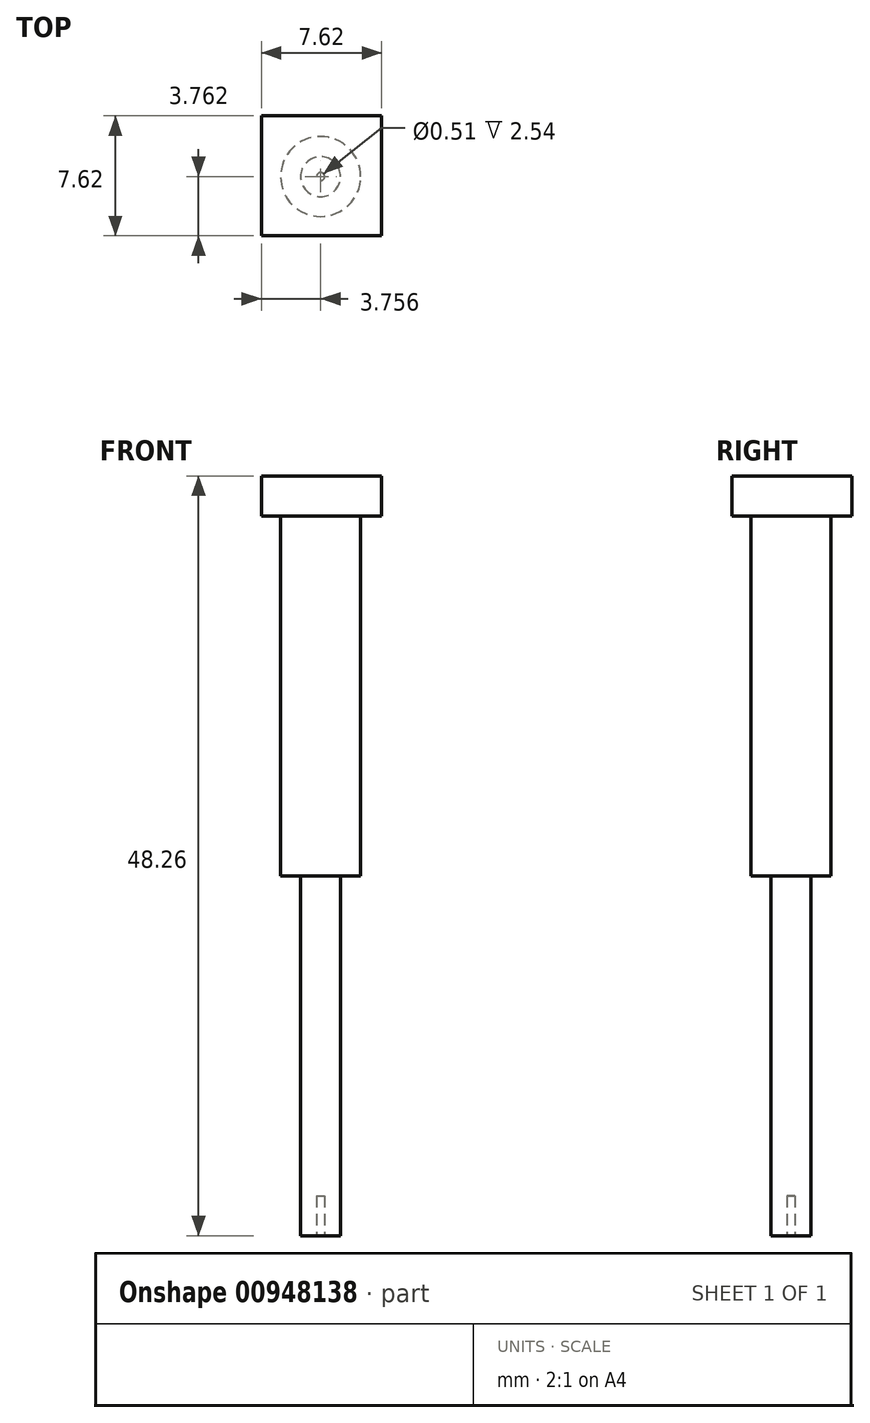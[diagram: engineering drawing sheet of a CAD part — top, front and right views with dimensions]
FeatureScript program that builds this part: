
annotation { "Feature Type Name" : "Feature", "Feature Type Description" : "" }
export const myFeature = defineFeature(function(context is Context, id is Id, definition is map)
    precondition{}
    {
        {
            var Q0;
            Q0=qCreatedBy(makeId("Top.planeOp"),FACE);
            var sketch = newSketch(context, id + "F0", { "sketchPlane" : qUnion([Q0])});
            skLineSegment(sketch, "E0.bottom", {"start": v(-42.6, -18.03) * mm, "end": v(-34.99, -18.03) * mm});
            skLineSegment(sketch, "E0.top", {"start": v(-42.6, -25.65) * mm, "end": v(-34.99, -25.65) * mm});
            skLineSegment(sketch, "E0.left", {"start": v(-42.6, -18.03) * mm, "end": v(-42.6, -25.65) * mm});
            skLineSegment(sketch, "E0.right", {"start": v(-34.99, -18.03) * mm, "end": v(-34.99, -25.65) * mm});
            skSolve(sketch);
        }
        {
            var Q0;
            Q0=qSketchRegion(id+"F0",true);
            var Q1;
            Q1 = qSketchRegion(id + "F2", true);
            extrude(context, id + "F1", {"entities" : qUnion([Q0, Q1]), "depth" : 2.54 * mm, "offsetDistance" : 25.4 * mm});
        }
        {
            var Q0;
            Q0=makeQuery(id+"F1.opExtrude","CAP_FACE",FACE,{"disambiguationData":[OSD([sQuery(id+"F0.wireOp",EDGE,"E0.bottom"),sQuery(id+"F0.wireOp",EDGE,"E0.top"),sQuery(id+"F0.wireOp",EDGE,"E0.left"),sQuery(id+"F0.wireOp",EDGE,"E0.right")])],"isStart":true});
            var sketch = newSketch(context, id + "F2", { "sketchPlane" : qUnion([Q0])});
            skCircle(sketch, "E1", {"center": v(-38.85, 21.89) * mm, "radius": 2.54 * mm});
            skCircle(sketch, "E2", {"center": v(-38.85, 21.89) * mm, "radius": 1.27 * mm});
            skSolve(sketch);
        }
        {
            var Q0;
            Q0=qSketchRegion(id+"F2",true);
            extrude(context, id + "F3", {"entities" : qUnion([Q0]), "operationType" : NewBodyOperationType.ADD, "depth" : 22.86 * mm, "offsetDistance" : 25.4 * mm});
        }
        {
            var Q0;
            Q0=makeQuery(id+"F3.boolean.opBoolean","SPLIT",FACE,{"disambiguationData":[TD([makeQuery(id+"F3.opExtrude","SWEPT_FACE",FACE,{"disambiguationData":[OSD([sQuery(id+"F2.wireOp",EDGE,"E2")])]})])],"derivedFrom":makeQuery(id+"F1.opExtrude","CAP_FACE",FACE,{"disambiguationData":[OSD([sQuery(id+"F0.wireOp",EDGE,"E0.bottom"),sQuery(id+"F0.wireOp",EDGE,"E0.top"),sQuery(id+"F0.wireOp",EDGE,"E0.left"),sQuery(id+"F0.wireOp",EDGE,"E0.right")])],"isStart":true})});
            extrude(context, id + "F4", {"entities" : qUnion([Q0]), "operationType" : NewBodyOperationType.ADD, "depth" : 22.86 * mm, "offsetDistance" : 25.4 * mm});
        }
        {
            var Q0;
            Q0=makeQuery(id+"F2.imprint","IMPRINT",FACE,{"disambiguationData":[TD([[makeQuery(id+"F2.imprint","IMPRINT",EDGE,{"derivedFrom":sQuery(id+"F2.wireOp",EDGE,"E2")}),1.0]])]});
            extrude(context, id + "F5", {"entities" : qUnion([Q0]), "operationType" : NewBodyOperationType.ADD, "depth" : 45.72 * mm, "offsetDistance" : 25.4 * mm});
        }
        {
            var Q0;
            Q0=makeQuery(id+"F5.opExtrude","CAP_FACE",FACE,{"disambiguationData":[OSD([sQuery(id+"F2.wireOp",EDGE,"E2")])],"isStart":false});
            var sketch = newSketch(context, id + "F6", { "sketchPlane" : qUnion([Q0])});
            skCircle(sketch, "E3", {"center": v(-38.85, 21.89) * mm, "radius": 0.25 * mm});
            skSolve(sketch);
        }
        {
            var Q0;
            Q0=makeQuery(id+"F6.imprint","IMPRINT",FACE,{"disambiguationData":[TD([[makeQuery(id+"F6.imprint","IMPRINT",EDGE,{"derivedFrom":sQuery(id+"F6.wireOp",EDGE,"E3")}),1.0]])]});
            extrude(context, id + "F7", {"entities" : qUnion([Q0]), "operationType" : NewBodyOperationType.REMOVE, "oppositeDirection" : true, "depth" : 2.54 * mm, "offsetDistance" : 25.4 * mm});
        }
    });
